# Revit family: Pump_Heavy_Duty-Solid_Handling-Zoeller-62_HD_Series (1)
name_source: partatom
category: Mechanical Equipment
units: mm (PartAtom-declared; Revit-internal decimal feet)

## family parameters
Always vertical = No
Cut with Voids When Loaded = No
OmniClass Number = 23.60.30.21
OmniClass Title = Pumps
Part Type = Normal
Room Calculation Point = No
Round Connector Dimension = Use Radius
Shared = Yes
Work Plane-Based = Yes

## types (10) — shared parameters
Assembly Code = D2010900
Default Elevation = 0"
Description = Commercial Effluent Pumps
Dry Pit (5-15 BHP) = Yes
Flange = ANSI B16.1
Height = 33 5/8"
Hertz = 60
High Temperature (5-10 BHP) = Yes
Impeller Type = Ductile Iron Semi-Open
Impeller Type (Optional) Bronze Semi-open = No
Impeller Type (Optional) Ductile Iron Vortex = No
Installation Type = Floor Mounted
Insulation = Class F
Inverter Duty Submersible (5-15 BHP Only) = No
Length = 18 3/8"
Manufacturer = Zoeller
Masterformat Number = 33 36 16
Masterformat Title = Utility Septic Tank Effluent Pumps
Material = Cast Iron-Zoeller-Powder Coated Epoxy
Max. Stator Temp. = 311 °F
Max. Water Temp. = 104 °F
Mechanical Seals = Tandem carbon/ceramic upper and silicon carbide/silicon carbide lower
Min. Recommended Fluid Level = 24"
Model = 6220-4"
Moisture Sensor (Optional) = Moisture Sensing Probes (Requires a circuit in control panel)
Motor Design Letter = NEMA B
Motor Shaft = 416 S.S.
Motor Thermal Shutoff (Single Phase Only) = Thermal Sensors With Automatic Reset
Motor Type = Standard Submersible
O-Rings (Optional) Viton = No
O-Rings and Cover Gasket = Buna-N
Omniclass Table 23 Code = 23.60.30.21
Omniclass Table 23 Title = Pumps
Operation = Non-Automatic
Power Cord = <20 = #12-4 SO (Models with a FLA greater than 36.7 amps use #8-4 gauge power cord; #4-4 for less than 36.7)
Price = Prices may vary. Please consult Manufacturer Representative for most up-to-date price list.
Product Page URL = http://www.zoellerengprod.com
RPM = 1750
Sensor Cord Size = #18-5
Shaft Seal Lower (Options) = Carbon/Silicon Carbide, Silicon Carbide/Silicon Carbide
Shaft Seal Upper (Options) = Silicon Carbide/Carbon, Silicon Carbide/Silicon Carbide
Shaft Seal Upper Standard = Carbon/Ceramic
Shipping Weight = 350lbs(159kg)
Solid Size = 3" (75 mm)
Tandem Seals = Standard
Type SOW Power Cord Length = 300"
URL = http://www.zoellerengprod.com
Voltage = 200-575
Warranty Information = 36 Months (Limited)
Waste Connection = Yes
Width = 14 11/16"

## per-type parameters (varying)
| type | Connecter Description | Discharge Diameter | Discharge Radius | Full Load Amps (Voltage Dependent) | Impeller Diameter | Locked Rotor Amps (Voltage Dependant) | Maximum KW Input | Motor | NEC Locked Rotor Code | Phase | Service Factor | Type | Void Visibility | Void Visibility 2 |
| 6220-4" | 4" Horizontal Discharge | 4" | 2" | 6.1-27.5 | 6 7/8" | 21.8-91 | 5.2 | 5.0 BHP | D | 1 or 3 | 1.2 | Permanent Split Capacitor or 3 Phase | -15" | 0" |
| 6221-4" | 4" Horizontal Discharge | 4" | 2" | 9.0-36.7 | 7 3/8" | 37.8-137 | 7.8 | 7.5 BHP | F | 1 or 3 | 1.2 | Permanent Split Capacitor or 3 Phase | -15" | 0" |
| 6222-4" | 4" Horizontal Discharge | 4" | 2" | 11.0-32.0 | 7 3/4" | 37.8-109 | 9.8 | 10.0 BHP | C | 3 | 1.2 | 3 Phase | -15" | 0" |
| 6224-4" | 4" Horizontal Discharge | 4" | 2" | 22.0-59.4 | 9 1/2" | 70.0-197 | 16.8 | 20.0 BHP | B | 3 | 1.0 | 3 Phase | -15" | 0" |
| 6224-6" | 6" Horizontal Discharge | 6" | 3" | 22.0-59.4 | 9 1/2" | 70.0-197 | 16.8 | 20.0 BHP | B | 3 | 1.0 | 3 Phase | -9 27/32" | 12" |
| 6221-6" | 6" Horizontal Discharge | 6" | 3" | 9.0-36.7 | 7 3/8" | 37.8-137 | 7.8 | 7.5 BHP | F | 1 or 3 | 1.2 | Permanent Split Capacitor or 3 Phase | -9 27/32" | 12" |
| 6220-6" | 6" Horizontal Discharge | 6" | 3" | 6.1-27.5 | 6 7/8" | 21.8-91 | 5.2 | 5.0 BHP | D | 1 or 3 | 1.2 | Permanent Split Capacitor or 3 Phase | -9 27/32" | 12" |
| 6222-6" | 6" Horizontal Discharge | 6" | 3" | 11.0-32.0 | 7 3/4" | 37.8-109 | 9.8 | 10.0 BHP | C | 3 | 1.2 | 3 Phase | -9 27/32" | 12" |
| 6223-4" | 4" Horizontal Discharge | 4" | 2" | 16.4-48.3 | 8 5/8" | 70-197 | 13.5 | 15.0 BHP | E | 3 | 1.2 | 3 Phase | -15" | 0" |
| 6223-6" | 6" Horizontal Discharge | 6" | 3" | 16.4-48.3 | 8 5/8" | 70-197 | 13.5 | 15.0 BHP | E | 3 | 1.2 | 3 Phase | -9 27/32" | 12" |

## geometry (parser evidence)
native form markers: Sweep x3
no freeform markers — native parametric forms only
